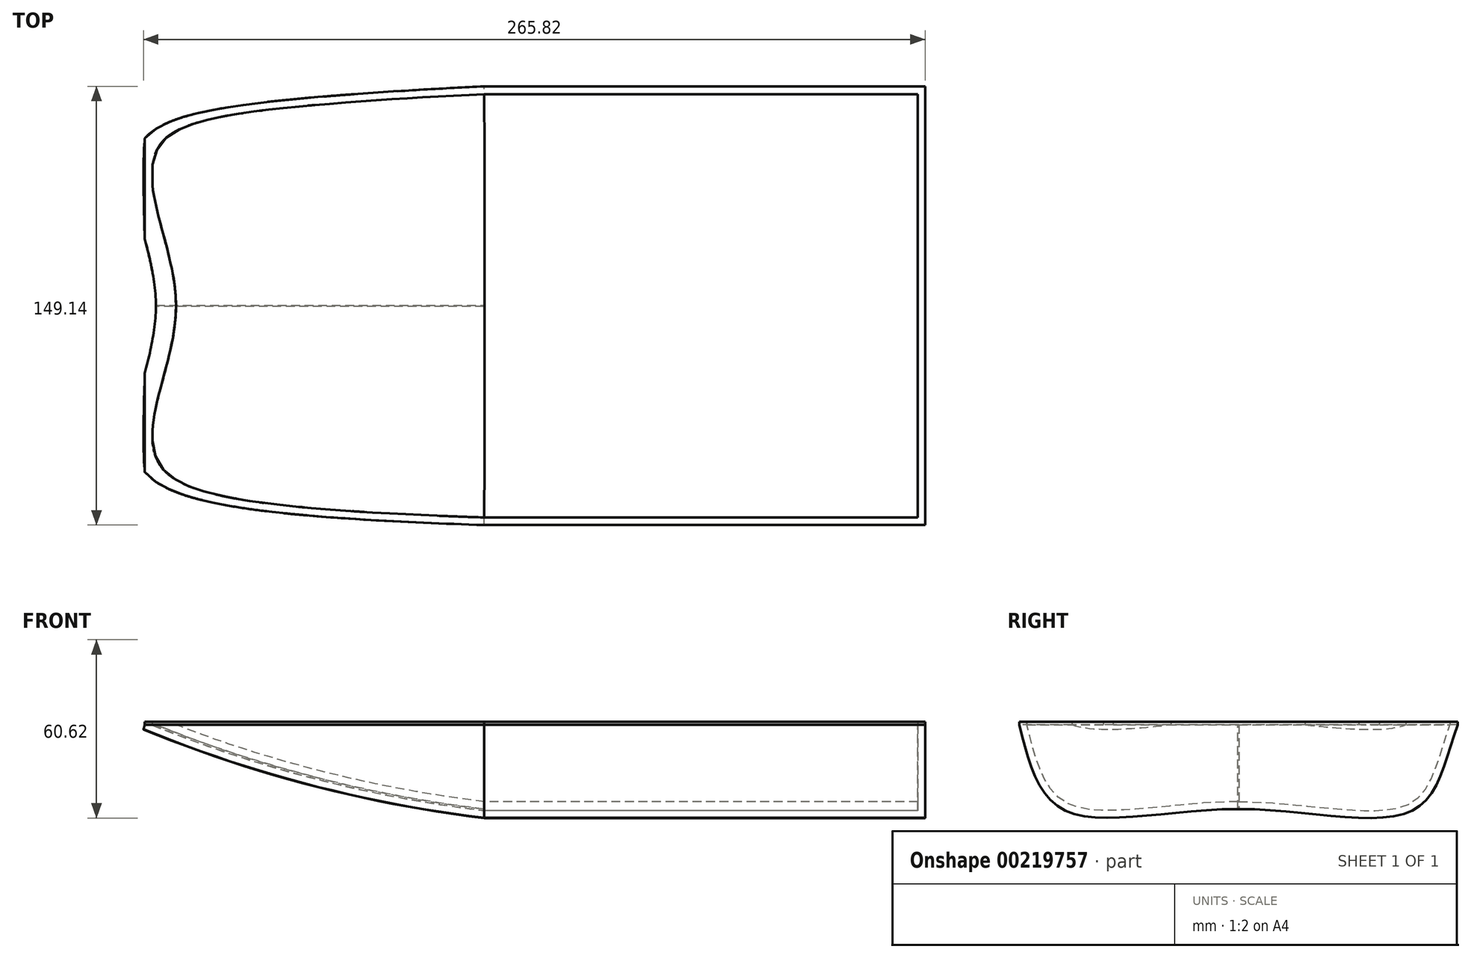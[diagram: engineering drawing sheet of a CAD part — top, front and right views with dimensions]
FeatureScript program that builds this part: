
annotation { "Feature Type Name" : "Feature", "Feature Type Description" : "" }
export const myFeature = defineFeature(function(context is Context, id is Id, definition is map)
    precondition{}
    {
        {
            var Q0;
            Q0=qCreatedBy(makeId("Front.planeOp"),FACE);
            var sketch = newSketch(context, id + "F0", { "sketchPlane" : qUnion([Q0])});
            skLineSegment(sketch, "E0.bottom", {"start": v(0, 0) * mm, "end": v(150, 0) * mm});
            skLineSegment(sketch, "E0.right", {"start": v(150, 0) * mm, "end": v(150, 30) * mm});
            skArc(sketch, "E1", {"start": v(-115, 30) * mm, "mid": v(-58.52, 11.1) * mm, "end": v(0, 0) * mm});
            skPoint(sketch, "E2.top.end.orphan", {"position": v(-115, 0) * mm});
            skSolve(sketch);
        }
        {
            var Q0;
            Q0=qCreatedBy(makeId("Right.planeOp"),FACE);
            cPlane(context, id + "F1", {"entities" : qUnion([Q0]), "cplaneType" : CPlaneType.OFFSET, "offset" : 150 * mm, "width" : 150 * mm, "height" : 150 * mm});
        }
        {
            var Q0;
            Q0=qCreatedBy(id+"F1.planeOp",FACE);
            var sketch = newSketch(context, id + "F2", { "sketchPlane" : qUnion([Q0])});
            skLineSegment(sketch, "E3.bottom", {"start": v(-75, 30) * mm, "end": v(75, 30) * mm});
            skLineSegment(sketch, "E3.top", {"start": v(-0.31, 0) * mm, "end": v(0, 0) * mm});
            skFitSpline(sketch, "E4", {"points": [v(-75, 30) * mm, v(-60, 0) * mm, v(0, 0) * mm, v(60, 0) * mm, v(75, 30) * mm], "startDerivative": vector(43.02, -173.66) * mm, "endDerivative": vector(65.03, 169.84) * mm});
            skPoint(sketch, "E5.orphan", {"position": v(-75, 0) * mm});
            skPoint(sketch, "E3.right.end.orphan", {"position": v(75, 0) * mm});
            skSolve(sketch);
        }
        {
            var Q0;
            {var subQ0=sQuery(id+"F2.wireOp",EDGE,"E3.bottom");Q0=makeQuery(id+"F2.imprint","IMPRINT",FACE,{"disambiguationData":[TD([[makeQuery(id+"F2.imprint","IMPRINT",EDGE,{"derivedFrom":subQ0}),-1.0]])]});}
            extrude(context, id + "F3", {"entities" : qUnion([Q0]), "oppositeDirection" : true, "depth" : 150 * mm});
        }
        {
            var Q0;
            Q0=makeQuery(id+"F3.opExtrude","CAP_FACE",FACE,{"disambiguationData":[OSD([sQuery(id+"F2.wireOp",EDGE,"E3.bottom"),sQuery(id+"F2.wireOp",EDGE,"E4")])],"isStart":false});
            var Q1;
            Q1=qSketchRegion(id+"F0",true);
            var Q2;
            Q2=sQuery(id+"F0.wireOp",EDGE,"E1");
            sweep(context, id + "F4", {"operationType" : NewBodyOperationType.ADD, "profiles" : qUnion([Q0, Q1]), "path" : qUnion([Q2])});
        }
        {
            var Q0;
            Q0=qCreatedBy(makeId("Front.planeOp"),FACE);
            var sketch = newSketch(context, id + "F5", { "sketchPlane" : qUnion([Q0])});
            skLineSegment(sketch, "E6.bottom", {"start": v(154.83, 28.62) * mm, "end": v(-132.64, 28.62) * mm});
            skLineSegment(sketch, "E6.top", {"start": v(154.83, 68.12) * mm, "end": v(-132.64, 68.12) * mm});
            skLineSegment(sketch, "E6.left", {"start": v(154.83, 28.62) * mm, "end": v(154.83, 68.12) * mm});
            skLineSegment(sketch, "E6.right", {"start": v(-132.64, 28.62) * mm, "end": v(-132.64, 68.12) * mm});
            skSolve(sketch);
        }
        {
            var Q0;
            Q0=qSketchRegion(id+"F5",true);
            extrude(context, id + "F6", {"entities" : qUnion([Q0]), "operationType" : NewBodyOperationType.REMOVE, "endBound" : BoundingType.SYMMETRIC, "oppositeDirection" : true, "depth" : 200 * mm});
        }
        {
            var Q0;
            Q0=makeQuery(id+"F6.boolean.opBoolean","COPY",FACE,{"derivedFrom":makeQuery(id+"F6.opExtrude","SWEPT_FACE",FACE,{"disambiguationData":[OSD([sQuery(id+"F5.wireOp",EDGE,"E6.bottom")])]})});
            shell(context, id + "F7", {"entities" : qUnion([Q0]), "thickness" : 2.5 * mm});
        }
        {
            var Q0;
            Q0=qCreatedBy(makeId("Top.planeOp"),FACE);
            cPlane(context, id + "F8", {"entities" : qUnion([Q0]), "cplaneType" : CPlaneType.OFFSET, "offset" : 30 * mm, "width" : 150 * mm, "height" : 150 * mm});
        }
        {
            var Q0;
            Q0=makeQuery(id+"F6.boolean.opBoolean","COPY",FACE,{"derivedFrom":makeQuery(id+"F6.opExtrude","SWEPT_FACE",FACE,{"disambiguationData":[OSD([sQuery(id+"F5.wireOp",EDGE,"E6.bottom")])]})});
            extrude(context, id + "F9", {"entities" : qUnion([Q0]), "operationType" : NewBodyOperationType.ADD, "depth" : 1 * mm});
        }
    });
